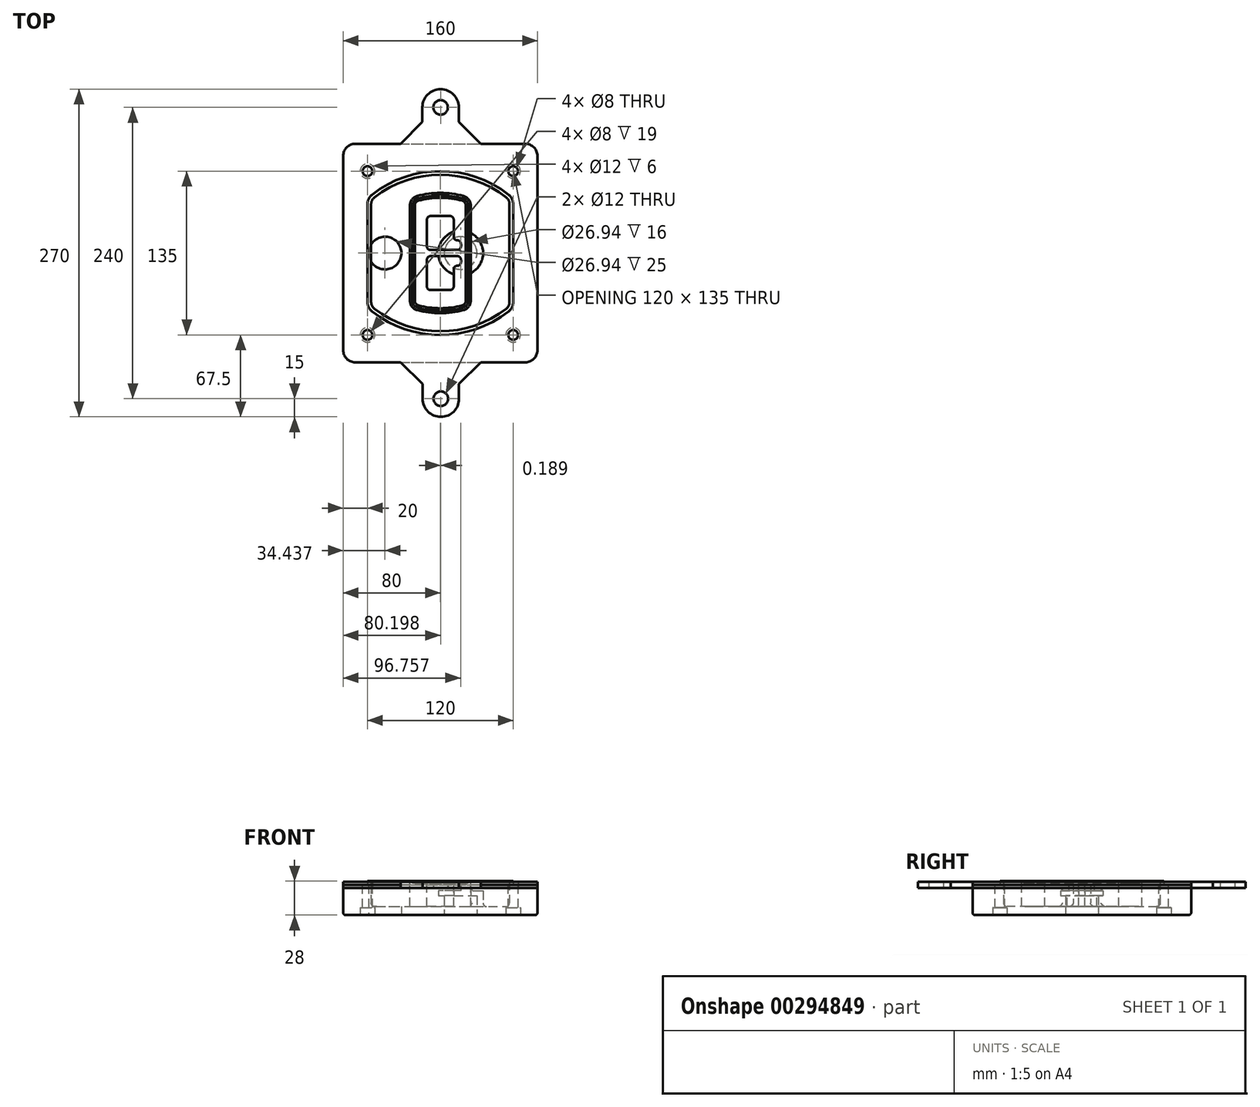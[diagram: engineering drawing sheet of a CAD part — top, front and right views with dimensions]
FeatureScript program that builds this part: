
annotation { "Feature Type Name" : "Feature", "Feature Type Description" : "" }
export const myFeature = defineFeature(function(context is Context, id is Id, definition is map)
    precondition{}
    {
        {
            var Q0;
            Q0=qCreatedBy(makeId("Top.planeOp"),FACE);
            var sketch = newSketch(context, id + "F0", { "sketchPlane" : qUnion([Q0])});
            skPoint(sketch, "E0.rect.middle", {"position": v(0, 0) * mm});
            skLineSegment(sketch, "E1.bottom", {"start": v(-70, -90) * mm, "end": v(70, -90) * mm});
            skLineSegment(sketch, "E1.top", {"start": v(-70, 90) * mm, "end": v(70, 90) * mm});
            skLineSegment(sketch, "E1.left", {"start": v(-80, -80) * mm, "end": v(-80, 80) * mm});
            skLineSegment(sketch, "E1.right", {"start": v(80, -80) * mm, "end": v(80, 80) * mm});
            skLineSegment(sketch, "E2", {"start": v(-80, 90) * mm, "end": v(80, -90) * mm, "construction": true});
            skLineSegment(sketch, "E3", {"start": v(80, 90) * mm, "end": v(-80, -90) * mm, "construction": true});
            skCircle(sketch, "E4", {"center": v(-60, 67.5) * mm, "radius": 4 * mm});
            skCircle(sketch, "E5", {"center": v(60, 67.5) * mm, "radius": 4 * mm});
            skCircle(sketch, "E6", {"center": v(60, -67.5) * mm, "radius": 4 * mm});
            skCircle(sketch, "E7", {"center": v(-60, -67.5) * mm, "radius": 4 * mm});
            skLineSegment(sketch, "E8", {"start": v(-60, 67.5) * mm, "end": v(60, 67.5) * mm, "construction": true});
            skLineSegment(sketch, "E9", {"start": v(60, 67.5) * mm, "end": v(60, -67.5) * mm, "construction": true});
            skLineSegment(sketch, "E10", {"start": v(60, -67.5) * mm, "end": v(-60, -67.5) * mm, "construction": true});
            skLineSegment(sketch, "E11", {"start": v(-60, -67.5) * mm, "end": v(-60, 67.5) * mm, "construction": true});
            skLineSegment(sketch, "E12", {"start": v(-60, 40.3) * mm, "end": v(-60, -40.3) * mm});
            skLineSegment(sketch, "E13", {"start": v(60, 40.3) * mm, "end": v(60, -40.3) * mm});
            skArc(sketch, "E14", {"start": v(56.15, 48.18) * mm, "mid": v(0, 67.5) * mm, "end": v(-56.15, 48.18) * mm});
            skArc(sketch, "E15", {"start": v(-56.15, -48.18) * mm, "mid": v(0, -67.5) * mm, "end": v(56.15, -48.18) * mm});
            skLineSegment(sketch, "E16", {"start": v(-60, 0) * mm, "end": v(60, 0) * mm, "construction": true});
            skPoint(sketch, "E17.visualSharp", {"position": v(-60, -45) * mm});
            skArc(sketch, "E17.filletArc", {"start": v(-60, -40.3) * mm, "mid": v(-58.99, -44.68) * mm, "end": v(-56.15, -48.18) * mm});
            skPoint(sketch, "E18.visualSharp", {"position": v(-60, 45) * mm});
            skArc(sketch, "E18.filletArc", {"start": v(-56.15, 48.18) * mm, "mid": v(-58.99, 44.68) * mm, "end": v(-60, 40.3) * mm});
            skPoint(sketch, "E19.visualSharp", {"position": v(60, 45) * mm});
            skArc(sketch, "E19.filletArc", {"start": v(60, 40.3) * mm, "mid": v(58.99, 44.68) * mm, "end": v(56.15, 48.18) * mm});
            skPoint(sketch, "E20.visualSharp", {"position": v(60, -45) * mm});
            skArc(sketch, "E20.filletArc", {"start": v(56.15, -48.18) * mm, "mid": v(58.99, -44.68) * mm, "end": v(60, -40.3) * mm});
            skPoint(sketch, "E21.visualSharp", {"position": v(-80, 90) * mm});
            skArc(sketch, "E21.filletArc", {"start": v(-70, 90) * mm, "mid": v(-77.07, 87.07) * mm, "end": v(-80, 80) * mm});
            skPoint(sketch, "E22.visualSharp", {"position": v(80, 90) * mm});
            skArc(sketch, "E22.filletArc", {"start": v(80, 80) * mm, "mid": v(77.07, 87.07) * mm, "end": v(70, 90) * mm});
            skPoint(sketch, "E23.visualSharp", {"position": v(80, -90) * mm});
            skArc(sketch, "E23.filletArc", {"start": v(70, -90) * mm, "mid": v(77.07, -87.07) * mm, "end": v(80, -80) * mm});
            skPoint(sketch, "E24.visualSharp", {"position": v(-80, -90) * mm});
            skArc(sketch, "E24.filletArc", {"start": v(-80, -80) * mm, "mid": v(-77.07, -87.07) * mm, "end": v(-70, -90) * mm});
            skArc(sketch, "E25.0", {"start": v(57, 40.3) * mm, "mid": v(56.3, 43.36) * mm, "end": v(54.3, 45.81) * mm});
            skLineSegment(sketch, "E25.1", {"start": v(57, 40.3) * mm, "end": v(57, -40.3) * mm});
            skArc(sketch, "E25.2", {"start": v(54.3, -45.81) * mm, "mid": v(56.3, -43.36) * mm, "end": v(57, -40.3) * mm});
            skArc(sketch, "E25.3", {"start": v(-54.3, -45.81) * mm, "mid": v(0, -64.5) * mm, "end": v(54.3, -45.81) * mm});
            skArc(sketch, "E25.4", {"start": v(-57, -40.3) * mm, "mid": v(-56.3, -43.36) * mm, "end": v(-54.3, -45.81) * mm});
            skArc(sketch, "E25.5", {"start": v(54.3, 45.81) * mm, "mid": v(0, 64.5) * mm, "end": v(-54.3, 45.81) * mm});
            skLineSegment(sketch, "E25.6", {"start": v(-57, 40.3) * mm, "end": v(-57, -40.3) * mm});
            skArc(sketch, "E25.7", {"start": v(-54.3, 45.81) * mm, "mid": v(-56.3, 43.36) * mm, "end": v(-57, 40.3) * mm});
            skArc(sketch, "E26.0", {"start": v(-58.62, 51.33) * mm, "mid": v(-62.58, 46.43) * mm, "end": v(-64, 40.3) * mm});
            skArc(sketch, "E26.1", {"start": v(58.62, 51.33) * mm, "mid": v(0, 71.5) * mm, "end": v(-58.62, 51.33) * mm});
            skArc(sketch, "E26.2", {"start": v(64, 40.3) * mm, "mid": v(62.58, 46.43) * mm, "end": v(58.62, 51.33) * mm});
            skLineSegment(sketch, "E26.3", {"start": v(64, 40.3) * mm, "end": v(64, -40.3) * mm});
            skArc(sketch, "E26.4", {"start": v(58.62, -51.33) * mm, "mid": v(62.58, -46.43) * mm, "end": v(64, -40.3) * mm});
            skLineSegment(sketch, "E26.5", {"start": v(-64, 40.3) * mm, "end": v(-64, -40.3) * mm});
            skArc(sketch, "E26.6", {"start": v(-58.62, -51.33) * mm, "mid": v(0, -71.5) * mm, "end": v(58.62, -51.33) * mm});
            skArc(sketch, "E26.7", {"start": v(-64, -40.3) * mm, "mid": v(-62.58, -46.43) * mm, "end": v(-58.62, -51.33) * mm});
            skSolve(sketch);
        }
        {
            var Q0;
            Q0=makeQuery(id+"F0.imprint","IMPRINT",FACE,{"disambiguationData":[TD([[makeQuery(id+"F0.imprint","IMPRINT",EDGE,{"derivedFrom":sQuery(id+"F0.wireOp",EDGE,"E1.bottom")}),1.0]])]});
            var Q1;
            Q1=makeQuery(id+"F0.imprint","IMPRINT",FACE,{"disambiguationData":[TD([[makeQuery(id+"F0.imprint","IMPRINT",EDGE,{"derivedFrom":sQuery(id+"F0.wireOp",EDGE,"E12")}),1.0]])]});
            var Q2;
            Q2=makeQuery(id+"F0.imprint","IMPRINT",FACE,{"disambiguationData":[TD([[makeQuery(id+"F0.imprint","IMPRINT",EDGE,{"derivedFrom":sQuery(id+"F0.wireOp",EDGE,"E25.0")}),1.0]])]});
            var Q3;
            Q3=makeQuery(id+"F0.imprint","IMPRINT",FACE,{"disambiguationData":[TD([[makeQuery(id+"F0.imprint","IMPRINT",EDGE,{"derivedFrom":sQuery(id+"F0.wireOp",EDGE,"E12")}),-1.0]])]});
            extrude(context, id + "F1", {"entities" : qUnion([Q0, Q1, Q2, Q3]), "oppositeDirection" : true, "depth" : 25 * mm});
        }
        {
            var Q0;
            Q0=makeQuery(id+"F0.imprint","IMPRINT",FACE,{"disambiguationData":[TD([[makeQuery(id+"F0.imprint","IMPRINT",EDGE,{"derivedFrom":sQuery(id+"F0.wireOp",EDGE,"E12")}),1.0]])]});
            extrude(context, id + "F2", {"entities" : qUnion([Q0]), "operationType" : NewBodyOperationType.ADD, "depth" : 3 * mm});
        }
        {
            var Q0;
            Q0=makeQuery(id+"F0.imprint","IMPRINT",FACE,{"disambiguationData":[TD([[makeQuery(id+"F0.imprint","IMPRINT",EDGE,{"derivedFrom":sQuery(id+"F0.wireOp",EDGE,"E25.0")}),1.0]])]});
            extrude(context, id + "F3", {"entities" : qUnion([Q0]), "operationType" : NewBodyOperationType.REMOVE, "oppositeDirection" : true, "depth" : 18 * mm});
        }
        {
            var Q0;
            Q0=makeQuery(id+"F2.opExtrude","CAP_FACE",FACE,{"disambiguationData":[OSD([sQuery(id+"F0.wireOp",EDGE,"E12"),sQuery(id+"F0.wireOp",EDGE,"E13"),sQuery(id+"F0.wireOp",EDGE,"E14"),sQuery(id+"F0.wireOp",EDGE,"E15"),sQuery(id+"F0.wireOp",EDGE,"E17.filletArc"),sQuery(id+"F0.wireOp",EDGE,"E18.filletArc"),sQuery(id+"F0.wireOp",EDGE,"E19.filletArc"),sQuery(id+"F0.wireOp",EDGE,"E20.filletArc"),sQuery(id+"F0.wireOp",EDGE,"E25.0"),sQuery(id+"F0.wireOp",EDGE,"E25.1"),sQuery(id+"F0.wireOp",EDGE,"E25.2"),sQuery(id+"F0.wireOp",EDGE,"E25.3"),sQuery(id+"F0.wireOp",EDGE,"E25.4"),sQuery(id+"F0.wireOp",EDGE,"E25.5"),sQuery(id+"F0.wireOp",EDGE,"E25.6"),sQuery(id+"F0.wireOp",EDGE,"E25.7")])],"isStart":false});
            var sketch = newSketch(context, id + "F4", { "sketchPlane" : qUnion([Q0])});
            skArc(sketch, "E27.0", {"start": v(-19.08, -46.97) * mm, "mid": v(0, -49.5) * mm, "end": v(19.08, -46.97) * mm});
            skArc(sketch, "E28.0", {"start": v(19.08, 46.97) * mm, "mid": v(0, 49.5) * mm, "end": v(-19.08, 46.97) * mm});
            skLineSegment(sketch, "E29", {"start": v(-25, 39.25) * mm, "end": v(-25, -39.25) * mm});
            skLineSegment(sketch, "E30", {"start": v(25, 39.25) * mm, "end": v(25, -39.25) * mm});
            skLineSegment(sketch, "E31", {"start": v(-25, 45.1) * mm, "end": v(25, 45.1) * mm, "construction": true});
            skLineSegment(sketch, "E32", {"start": v(-25, -45.1) * mm, "end": v(25, -45.1) * mm, "construction": true});
            skPoint(sketch, "E33.visualSharp", {"position": v(-25, 45.1) * mm});
            skArc(sketch, "E33.filletArc", {"start": v(-19.08, 46.97) * mm, "mid": v(-23.35, 44.11) * mm, "end": v(-25, 39.25) * mm});
            skPoint(sketch, "E34.visualSharp", {"position": v(25, 45.1) * mm});
            skArc(sketch, "E34.filletArc", {"start": v(25, 39.25) * mm, "mid": v(23.35, 44.11) * mm, "end": v(19.08, 46.97) * mm});
            skPoint(sketch, "E35.visualSharp", {"position": v(25, -45.1) * mm});
            skArc(sketch, "E35.filletArc", {"start": v(19.08, -46.97) * mm, "mid": v(23.35, -44.11) * mm, "end": v(25, -39.25) * mm});
            skPoint(sketch, "E36.visualSharp", {"position": v(-25, -45.1) * mm});
            skArc(sketch, "E36.filletArc", {"start": v(-25, -39.25) * mm, "mid": v(-23.35, -44.11) * mm, "end": v(-19.08, -46.97) * mm});
            skArc(sketch, "E37.0", {"start": v(54.3, 45.81) * mm, "mid": v(0, 64.5) * mm, "end": v(-54.3, 45.81) * mm});
            skArc(sketch, "E37.1", {"start": v(-54.3, 45.81) * mm, "mid": v(-56.3, 43.36) * mm, "end": v(-57, 40.3) * mm});
            skLineSegment(sketch, "E37.2", {"start": v(-57, 40.3) * mm, "end": v(-57, -40.3) * mm});
            skArc(sketch, "E37.3", {"start": v(-57, -40.3) * mm, "mid": v(-56.3, -43.36) * mm, "end": v(-54.3, -45.81) * mm});
            skArc(sketch, "E37.4", {"start": v(-54.3, -45.81) * mm, "mid": v(0, -64.5) * mm, "end": v(54.3, -45.81) * mm});
            skArc(sketch, "E37.5", {"start": v(54.3, -45.81) * mm, "mid": v(56.3, -43.36) * mm, "end": v(57, -40.3) * mm});
            skLineSegment(sketch, "E37.6", {"start": v(57, 40.3) * mm, "end": v(57, -40.3) * mm});
            skArc(sketch, "E37.7", {"start": v(57, 40.3) * mm, "mid": v(56.3, 43.36) * mm, "end": v(54.3, 45.81) * mm});
            skLineSegment(sketch, "E38.0", {"start": v(23, 39.25) * mm, "end": v(23, -39.25) * mm});
            skArc(sketch, "E38.1", {"start": v(18.56, -45.04) * mm, "mid": v(21.76, -42.9) * mm, "end": v(23, -39.25) * mm});
            skArc(sketch, "E38.2", {"start": v(-18.56, -45.04) * mm, "mid": v(0, -47.5) * mm, "end": v(18.56, -45.04) * mm});
            skArc(sketch, "E38.3", {"start": v(-23, -39.25) * mm, "mid": v(-21.76, -42.9) * mm, "end": v(-18.56, -45.04) * mm});
            skLineSegment(sketch, "E38.4", {"start": v(-23, 39.25) * mm, "end": v(-23, -39.25) * mm});
            skArc(sketch, "E38.5", {"start": v(23, 39.25) * mm, "mid": v(21.76, 42.9) * mm, "end": v(18.56, 45.04) * mm});
            skArc(sketch, "E38.6", {"start": v(-18.56, 45.04) * mm, "mid": v(-21.76, 42.9) * mm, "end": v(-23, 39.25) * mm});
            skArc(sketch, "E38.7", {"start": v(18.56, 45.04) * mm, "mid": v(0, 47.5) * mm, "end": v(-18.56, 45.04) * mm});
            skArc(sketch, "E39.0", {"start": v(21, 39.25) * mm, "mid": v(20.18, 41.68) * mm, "end": v(18.04, 43.1) * mm});
            skLineSegment(sketch, "E39.1", {"start": v(21, 39.25) * mm, "end": v(21, -39.25) * mm});
            skArc(sketch, "E39.2", {"start": v(18.04, -43.1) * mm, "mid": v(20.18, -41.68) * mm, "end": v(21, -39.25) * mm});
            skArc(sketch, "E39.3", {"start": v(-18.04, -43.1) * mm, "mid": v(0, -45.5) * mm, "end": v(18.04, -43.1) * mm});
            skArc(sketch, "E39.4", {"start": v(-21, -39.25) * mm, "mid": v(-20.18, -41.68) * mm, "end": v(-18.04, -43.1) * mm});
            skArc(sketch, "E39.5", {"start": v(18.04, 43.1) * mm, "mid": v(0, 45.5) * mm, "end": v(-18.04, 43.1) * mm});
            skLineSegment(sketch, "E39.6", {"start": v(-21, 39.25) * mm, "end": v(-21, -39.25) * mm});
            skArc(sketch, "E39.7", {"start": v(-18.04, 43.1) * mm, "mid": v(-20.18, 41.68) * mm, "end": v(-21, 39.25) * mm});
            skLineSegment(sketch, "E40", {"start": v(-25, 0) * mm, "end": v(25, 0) * mm, "construction": true});
            skLineSegment(sketch, "E41", {"start": v(-11, 5.5) * mm, "end": v(-11, 27.5) * mm});
            skLineSegment(sketch, "E42", {"start": v(-8, 30.5) * mm, "end": v(8, 30.5) * mm});
            skLineSegment(sketch, "E43", {"start": v(11, 27.5) * mm, "end": v(11, 13.5) * mm});
            skLineSegment(sketch, "E44", {"start": v(14, 10.5) * mm, "end": v(14, 10.5) * mm});
            skLineSegment(sketch, "E45", {"start": v(17, 7.5) * mm, "end": v(17, 5.5) * mm});
            skLineSegment(sketch, "E46", {"start": v(14, 2.5) * mm, "end": v(-8, 2.5) * mm});
            skPoint(sketch, "E47.visualSharp", {"position": v(-11, 30.5) * mm});
            skArc(sketch, "E47.filletArc", {"start": v(-8, 30.5) * mm, "mid": v(-10.12, 29.62) * mm, "end": v(-11, 27.5) * mm});
            skPoint(sketch, "E48.visualSharp", {"position": v(11, 30.5) * mm});
            skArc(sketch, "E48.filletArc", {"start": v(11, 27.5) * mm, "mid": v(10.12, 29.62) * mm, "end": v(8, 30.5) * mm});
            skPoint(sketch, "E49.visualSharp", {"position": v(11, 10.5) * mm});
            skArc(sketch, "E49.filletArc", {"start": v(11, 13.5) * mm, "mid": v(11.88, 11.38) * mm, "end": v(14, 10.5) * mm});
            skPoint(sketch, "E50.visualSharp", {"position": v(17, 10.5) * mm});
            skArc(sketch, "E50.filletArc", {"start": v(17, 7.5) * mm, "mid": v(16.12, 9.62) * mm, "end": v(14, 10.5) * mm});
            skPoint(sketch, "E51.visualSharp", {"position": v(17, 2.5) * mm});
            skArc(sketch, "E51.filletArc", {"start": v(14, 2.5) * mm, "mid": v(16.12, 3.38) * mm, "end": v(17, 5.5) * mm});
            skPoint(sketch, "E52.visualSharp", {"position": v(-11, 2.5) * mm});
            skArc(sketch, "E52.filletArc", {"start": v(-11, 5.5) * mm, "mid": v(-10.12, 3.38) * mm, "end": v(-8, 2.5) * mm});
            skLineSegment(sketch, "E53.0.MirrorCS", {"start": v(14, -2.5) * mm, "end": v(-8, -2.5) * mm});
            skArc(sketch, "E54.0.MirrorCS", {"start": v(-11, -5.5) * mm, "mid": v(-10.12, -3.38) * mm, "end": v(-8, -2.5) * mm});
            skLineSegment(sketch, "E55.0.MirrorCS", {"start": v(-11, -5.5) * mm, "end": v(-11, -27.5) * mm});
            skArc(sketch, "E56.0.MirrorCS", {"start": v(-8, -30.5) * mm, "mid": v(-10.12, -29.62) * mm, "end": v(-11, -27.5) * mm});
            skLineSegment(sketch, "E57.0.MirrorCS", {"start": v(-8, -30.5) * mm, "end": v(8, -30.5) * mm});
            skArc(sketch, "E58.0.MirrorCS", {"start": v(11, -27.5) * mm, "mid": v(10.12, -29.62) * mm, "end": v(8, -30.5) * mm});
            skLineSegment(sketch, "E59.0.MirrorCS", {"start": v(11, -27.5) * mm, "end": v(11, -13.5) * mm});
            skArc(sketch, "E60.0.MirrorCS", {"start": v(11, -13.5) * mm, "mid": v(11.88, -11.38) * mm, "end": v(14, -10.5) * mm});
            skArc(sketch, "E61.0.MirrorCS", {"start": v(17, -7.5) * mm, "mid": v(16.12, -9.62) * mm, "end": v(14, -10.5) * mm});
            skLineSegment(sketch, "E62.0.MirrorCS", {"start": v(17, -7.5) * mm, "end": v(17, -5.5) * mm});
            skArc(sketch, "E63.0.MirrorCS", {"start": v(14, -2.5) * mm, "mid": v(16.12, -3.38) * mm, "end": v(17, -5.5) * mm});
            skSolve(sketch);
        }
        {
            var Q0;
            Q0=makeQuery(id+"F4.imprint","IMPRINT",FACE,{"disambiguationData":[TD([[makeQuery(id+"F4.imprint","IMPRINT",EDGE,{"derivedFrom":sQuery(id+"F4.wireOp",EDGE,"E27.0")}),1.0]])]});
            var Q1;
            Q1=makeQuery(id+"F4.imprint","IMPRINT",FACE,{"disambiguationData":[TD([[makeQuery(id+"F4.imprint","IMPRINT",EDGE,{"derivedFrom":sQuery(id+"F4.wireOp",EDGE,"E38.0")}),-1.0]])]});
            var Q2;
            Q2=makeQuery(id+"F4.imprint","IMPRINT",FACE,{"disambiguationData":[TD([[makeQuery(id+"F4.imprint","IMPRINT",EDGE,{"derivedFrom":sQuery(id+"F4.wireOp",EDGE,"E39.0")}),1.0]])]});
            extrude(context, id + "F5", {"entities" : qUnion([Q0, Q1, Q2]), "operationType" : NewBodyOperationType.ADD, "endBound" : BoundingType.UP_TO_NEXT, "oppositeDirection" : true, "depth" : 25 * mm});
        }
        {
            var Q0;
            Q0=makeQuery(id+"F4.imprint","IMPRINT",FACE,{"disambiguationData":[TD([[makeQuery(id+"F4.imprint","IMPRINT",EDGE,{"derivedFrom":sQuery(id+"F4.wireOp",EDGE,"E38.0")}),-1.0]])]});
            extrude(context, id + "F6", {"entities" : qUnion([Q0]), "operationType" : NewBodyOperationType.REMOVE, "oppositeDirection" : true, "depth" : 2 * mm});
        }
        {
            var Q0;
            Q0=makeQuery(id+"F1.opExtrude","CAP_FACE",FACE,{"disambiguationData":[OSD([sQuery(id+"F0.wireOp",EDGE,"E1.bottom"),sQuery(id+"F0.wireOp",EDGE,"E1.top"),sQuery(id+"F0.wireOp",EDGE,"E1.left"),sQuery(id+"F0.wireOp",EDGE,"E1.right"),sQuery(id+"F0.wireOp",EDGE,"E4"),sQuery(id+"F0.wireOp",EDGE,"E5"),sQuery(id+"F0.wireOp",EDGE,"E6"),sQuery(id+"F0.wireOp",EDGE,"E7"),sQuery(id+"F0.wireOp",EDGE,"E21.filletArc"),sQuery(id+"F0.wireOp",EDGE,"E22.filletArc"),sQuery(id+"F0.wireOp",EDGE,"E23.filletArc"),sQuery(id+"F0.wireOp",EDGE,"E24.filletArc")])],"isStart":false});
            var sketch = newSketch(context, id + "F7", { "sketchPlane" : qUnion([Q0])});
            skCircle(sketch, "E64", {"center": v(16.76, 0) * mm, "radius": 13.47 * mm});
            skCircle(sketch, "E65", {"center": v(-45.56, 0) * mm, "radius": 13.47 * mm});
            skLineSegment(sketch, "E66", {"start": v(80, 0) * mm, "end": v(-80, 0) * mm});
            skCircle(sketch, "E67", {"center": v(16.76, 0) * mm, "radius": 18.47 * mm});
            skCircle(sketch, "E68", {"center": v(60, -67.5) * mm, "radius": 6 * mm});
            skCircle(sketch, "E69", {"center": v(-60, -67.5) * mm, "radius": 6 * mm});
            skCircle(sketch, "E70", {"center": v(-60, 67.5) * mm, "radius": 6 * mm});
            skCircle(sketch, "E71", {"center": v(60, 67.5) * mm, "radius": 6 * mm});
            skSolve(sketch);
        }
        {
            var Q0;
            {var subQ1=sQuery(id+"F7.wireOp",EDGE,"E66");var subQ4=sQuery(id+"F7.wireOp",EDGE,"E64");var subQ6=makeQuery(id+"F7.imprint","INTERSECT",VERTEX,{"disambiguationData":[OD(0.0)],"derivedFrom":[subQ4,subQ1]});Q0=makeQuery(id+"F7.imprint","IMPRINT",FACE,{"disambiguationData":[TD([[makeQuery(id+"F7.imprint","IMPRINT",EDGE,{"disambiguationData":[TD([[subQ6,-1.0]])],"derivedFrom":subQ4}),-1.0]])]});}
            var Q1;
            {var subQ0=sQuery(id+"F7.wireOp",EDGE,"E66");var subQ1=sQuery(id+"F7.wireOp",EDGE,"E64");var subQ3=makeQuery(id+"F7.imprint","INTERSECT",VERTEX,{"disambiguationData":[OD(0.0)],"derivedFrom":[subQ1,subQ0]});Q1=makeQuery(id+"F7.imprint","IMPRINT",FACE,{"disambiguationData":[TD([[makeQuery(id+"F7.imprint","IMPRINT",EDGE,{"disambiguationData":[TD([[subQ3,-1.0]])],"derivedFrom":subQ1}),1.0]])]});}
            var Q2;
            {var subQ0=sQuery(id+"F7.wireOp",EDGE,"E66");var subQ1=sQuery(id+"F7.wireOp",EDGE,"E64");var subQ3=makeQuery(id+"F7.imprint","INTERSECT",VERTEX,{"disambiguationData":[OD(0.0)],"derivedFrom":[subQ1,subQ0]});Q2=makeQuery(id+"F7.imprint","IMPRINT",FACE,{"disambiguationData":[TD([[makeQuery(id+"F7.imprint","IMPRINT",EDGE,{"disambiguationData":[TD([[subQ3,1.0]])],"derivedFrom":subQ1}),1.0]])]});}
            var Q3;
            {var subQ1=sQuery(id+"F7.wireOp",EDGE,"E66");var subQ4=sQuery(id+"F7.wireOp",EDGE,"E64");var subQ6=makeQuery(id+"F7.imprint","INTERSECT",VERTEX,{"disambiguationData":[OD(0.0)],"derivedFrom":[subQ4,subQ1]});Q3=makeQuery(id+"F7.imprint","IMPRINT",FACE,{"disambiguationData":[TD([[makeQuery(id+"F7.imprint","IMPRINT",EDGE,{"disambiguationData":[TD([[subQ6,1.0]])],"derivedFrom":subQ4}),-1.0]])]});}
            extrude(context, id + "F8", {"entities" : qUnion([Q0, Q1, Q2, Q3]), "operationType" : NewBodyOperationType.ADD, "oppositeDirection" : true, "depth" : 20 * mm});
        }
        {
            var Q0;
            {var subQ0=sQuery(id+"F7.wireOp",EDGE,"E66");var subQ1=sQuery(id+"F7.wireOp",EDGE,"E64");var subQ3=makeQuery(id+"F7.imprint","INTERSECT",VERTEX,{"disambiguationData":[OD(0.0)],"derivedFrom":[subQ1,subQ0]});Q0=makeQuery(id+"F7.imprint","IMPRINT",FACE,{"disambiguationData":[TD([[makeQuery(id+"F7.imprint","IMPRINT",EDGE,{"disambiguationData":[TD([[subQ3,-1.0]])],"derivedFrom":subQ1}),1.0]])]});}
            var Q1;
            {var subQ0=sQuery(id+"F7.wireOp",EDGE,"E66");var subQ1=sQuery(id+"F7.wireOp",EDGE,"E64");var subQ3=makeQuery(id+"F7.imprint","INTERSECT",VERTEX,{"disambiguationData":[OD(0.0)],"derivedFrom":[subQ1,subQ0]});Q1=makeQuery(id+"F7.imprint","IMPRINT",FACE,{"disambiguationData":[TD([[makeQuery(id+"F7.imprint","IMPRINT",EDGE,{"disambiguationData":[TD([[subQ3,1.0]])],"derivedFrom":subQ1}),1.0]])]});}
            extrude(context, id + "F9", {"entities" : qUnion([Q0, Q1]), "operationType" : NewBodyOperationType.REMOVE, "oppositeDirection" : true, "depth" : 16 * mm});
        }
        {
            var Q0;
            {var subQ0=sQuery(id+"F7.wireOp",EDGE,"E66");var subQ1=sQuery(id+"F7.wireOp",EDGE,"E65");var subQ3=makeQuery(id+"F7.imprint","INTERSECT",VERTEX,{"disambiguationData":[OD(0.0)],"derivedFrom":[subQ1,subQ0]});Q0=makeQuery(id+"F7.imprint","IMPRINT",FACE,{"disambiguationData":[TD([[makeQuery(id+"F7.imprint","IMPRINT",EDGE,{"disambiguationData":[TD([[subQ3,-1.0]])],"derivedFrom":subQ1}),1.0]])]});}
            var Q1;
            {var subQ0=sQuery(id+"F7.wireOp",EDGE,"E66");var subQ1=sQuery(id+"F7.wireOp",EDGE,"E65");var subQ3=makeQuery(id+"F7.imprint","INTERSECT",VERTEX,{"disambiguationData":[OD(0.0)],"derivedFrom":[subQ1,subQ0]});Q1=makeQuery(id+"F7.imprint","IMPRINT",FACE,{"disambiguationData":[TD([[makeQuery(id+"F7.imprint","IMPRINT",EDGE,{"disambiguationData":[TD([[subQ3,1.0]])],"derivedFrom":subQ1}),1.0]])]});}
            extrude(context, id + "F10", {"entities" : qUnion([Q0, Q1]), "operationType" : NewBodyOperationType.REMOVE, "oppositeDirection" : true, "depth" : 25 * mm});
        }
        {
            var Q0;
            Q0=makeQuery(id+"F7.imprint","IMPRINT",FACE,{"disambiguationData":[TD([[makeQuery(id+"F7.imprint","IMPRINT",EDGE,{"derivedFrom":sQuery(id+"F7.wireOp",EDGE,"E68")}),1.0]])]});
            var Q1;
            Q1=makeQuery(id+"F7.imprint","IMPRINT",FACE,{"disambiguationData":[TD([[makeQuery(id+"F7.imprint","IMPRINT",EDGE,{"derivedFrom":makeQuery(id+"F1.opExtrude","CAP_EDGE",EDGE,{"disambiguationData":[OSD([sQuery(id+"F0.wireOp",EDGE,"E5")])],"isStart":false})}),-1.0]])]});
            var Q2;
            Q2=makeQuery(id+"F7.imprint","IMPRINT",FACE,{"disambiguationData":[TD([[makeQuery(id+"F7.imprint","IMPRINT",EDGE,{"derivedFrom":sQuery(id+"F7.wireOp",EDGE,"E69")}),1.0]])]});
            var Q3;
            Q3=makeQuery(id+"F7.imprint","IMPRINT",FACE,{"disambiguationData":[TD([[makeQuery(id+"F7.imprint","IMPRINT",EDGE,{"derivedFrom":makeQuery(id+"F1.opExtrude","CAP_EDGE",EDGE,{"disambiguationData":[OSD([sQuery(id+"F0.wireOp",EDGE,"E4")])],"isStart":false})}),-1.0]])]});
            var Q4;
            Q4=makeQuery(id+"F7.imprint","IMPRINT",FACE,{"disambiguationData":[TD([[makeQuery(id+"F7.imprint","IMPRINT",EDGE,{"derivedFrom":sQuery(id+"F7.wireOp",EDGE,"E70")}),1.0]])]});
            var Q5;
            Q5=makeQuery(id+"F7.imprint","IMPRINT",FACE,{"disambiguationData":[TD([[makeQuery(id+"F7.imprint","IMPRINT",EDGE,{"derivedFrom":makeQuery(id+"F1.opExtrude","CAP_EDGE",EDGE,{"disambiguationData":[OSD([sQuery(id+"F0.wireOp",EDGE,"E7")])],"isStart":false})}),-1.0]])]});
            var Q6;
            Q6=makeQuery(id+"F7.imprint","IMPRINT",FACE,{"disambiguationData":[TD([[makeQuery(id+"F7.imprint","IMPRINT",EDGE,{"derivedFrom":sQuery(id+"F7.wireOp",EDGE,"E71")}),1.0]])]});
            var Q7;
            Q7=makeQuery(id+"F7.imprint","IMPRINT",FACE,{"disambiguationData":[TD([[makeQuery(id+"F7.imprint","IMPRINT",EDGE,{"derivedFrom":makeQuery(id+"F1.opExtrude","CAP_EDGE",EDGE,{"disambiguationData":[OSD([sQuery(id+"F0.wireOp",EDGE,"E6")])],"isStart":false})}),-1.0]])]});
            extrude(context, id + "F11", {"entities" : qUnion([Q0, Q1, Q2, Q3, Q4, Q5, Q6, Q7]), "operationType" : NewBodyOperationType.REMOVE, "oppositeDirection" : true, "depth" : 6 * mm});
        }
        {
            var Q0;
            Q0=makeQuery(id+"F9.boolean.opBoolean","COPY",FACE,{"derivedFrom":makeQuery(id+"F9.opExtrude","CAP_FACE",FACE,{"disambiguationData":[OSD([sQuery(id+"F7.wireOp",EDGE,"E64")])],"isStart":false})});
            var sketch = newSketch(context, id + "F12", { "sketchPlane" : qUnion([Q0])});
            skArc(sketch, "E72.0", {"start": v(11, 17.55) * mm, "mid": v(2.57, 11.82) * mm, "end": v(-1.54, 2.5) * mm});
            skArc(sketch, "E72.1", {"start": v(-1.54, -2.5) * mm, "mid": v(2.57, -11.82) * mm, "end": v(11, -17.55) * mm});
            skLineSegment(sketch, "E73", {"start": v(-1.54, -2.5) * mm, "end": v(14, -2.5) * mm});
            skLineSegment(sketch, "E74.0", {"start": v(14, 2.5) * mm, "end": v(-1.54, 2.5) * mm});
            skArc(sketch, "E74.1", {"start": v(14, 2.5) * mm, "mid": v(16.12, 3.38) * mm, "end": v(17, 5.5) * mm});
            skLineSegment(sketch, "E74.2", {"start": v(17, 7.5) * mm, "end": v(17, 5.5) * mm});
            skArc(sketch, "E74.3", {"start": v(17, 7.5) * mm, "mid": v(16.12, 9.62) * mm, "end": v(14, 10.5) * mm});
            skArc(sketch, "E74.4", {"start": v(11, 13.5) * mm, "mid": v(11.88, 11.38) * mm, "end": v(14, 10.5) * mm});
            skLineSegment(sketch, "E74.5", {"start": v(11, 17.55) * mm, "end": v(11, 13.5) * mm});
            skLineSegment(sketch, "E74.7", {"start": v(14, -2.5) * mm, "end": v(-1.54, -2.5) * mm});
            skArc(sketch, "E74.8", {"start": v(14, -2.5) * mm, "mid": v(16.12, -3.38) * mm, "end": v(17, -5.5) * mm});
            skLineSegment(sketch, "E74.9", {"start": v(17, -7.5) * mm, "end": v(17, -5.5) * mm});
            skArc(sketch, "E74.10", {"start": v(17, -7.5) * mm, "mid": v(16.12, -9.62) * mm, "end": v(14, -10.5) * mm});
            skArc(sketch, "E74.11", {"start": v(11, -13.5) * mm, "mid": v(11.88, -11.38) * mm, "end": v(14, -10.5) * mm});
            skLineSegment(sketch, "E74.12", {"start": v(11, -17.55) * mm, "end": v(11, -13.5) * mm});
            skPoint(sketch, "E75.orphan", {"position": v(11, -27.5) * mm});
            skPoint(sketch, "E76.orphan", {"position": v(-8, -2.5) * mm});
            skPoint(sketch, "E77.orphan", {"position": v(-8, 2.5) * mm});
            skPoint(sketch, "E78.orphan", {"position": v(11, 27.5) * mm});
            skSolve(sketch);
        }
        {
            var Q0;
            {var subQ7=sQuery(id+"F12.wireOp",EDGE,"E72.0");var subQ14=sQuery(id+"F12.wireOp",EDGE,"E72.1");var subQ16=sQuery(id+"F12.wireOp",EDGE,"E74.1");var subQ18=sQuery(id+"F12.wireOp",EDGE,"E74.8");Q0=qUnion([makeQuery(id+"F12.imprint","IMPRINT",FACE,{"disambiguationData":[TD([[makeQuery(id+"F12.imprint","IMPRINT",EDGE,{"derivedFrom":subQ7}),1.0]])]}),makeQuery(id+"F12.imprint","IMPRINT",FACE,{"disambiguationData":[TD([[makeQuery(id+"F12.imprint","IMPRINT",EDGE,{"derivedFrom":subQ14}),1.0]])]}),makeQuery(id+"F12.imprint","IMPRINT",FACE,{"disambiguationData":[TD([[makeQuery(id+"F12.imprint","IMPRINT",EDGE,{"derivedFrom":subQ16}),1.0]])]}),makeQuery(id+"F12.imprint","IMPRINT",FACE,{"disambiguationData":[TD([[makeQuery(id+"F12.imprint","IMPRINT",EDGE,{"derivedFrom":subQ18}),-1.0]])]})]);}
            var Q1;
            Q1=makeQuery(id+"F5.boolean.opBoolean","SPLIT",FACE,{"disambiguationData":[TD([makeQuery(id+"F5.opExtrude","SWEPT_FACE",FACE,{"disambiguationData":[OSD([sQuery(id+"F4.wireOp",EDGE,"E41")])]})])],"derivedFrom":makeQuery(id+"F3.boolean.opBoolean","COPY",FACE,{"derivedFrom":makeQuery(id+"F3.opExtrude","CAP_FACE",FACE,{"disambiguationData":[OSD([sQuery(id+"F0.wireOp",EDGE,"E25.0"),sQuery(id+"F0.wireOp",EDGE,"E25.1"),sQuery(id+"F0.wireOp",EDGE,"E25.2"),sQuery(id+"F0.wireOp",EDGE,"E25.3"),sQuery(id+"F0.wireOp",EDGE,"E25.4"),sQuery(id+"F0.wireOp",EDGE,"E25.5"),sQuery(id+"F0.wireOp",EDGE,"E25.6"),sQuery(id+"F0.wireOp",EDGE,"E25.7")])],"isStart":false})})});
            extrude(context, id + "F13", {"entities" : qUnion([Q0]), "operationType" : NewBodyOperationType.REMOVE, "endBound" : BoundingType.UP_TO_SURFACE, "endBoundEntityFace" : qUnion([Q1]), "depth" : 25 * mm});
        }
        {
            var Q0;
            Q0=makeQuery(id+"F3.boolean.opBoolean","COPY",EDGE,{"derivedFrom":makeQuery(id+"F3.opExtrude","CAP_EDGE",EDGE,{"disambiguationData":[OSD([sQuery(id+"F0.wireOp",EDGE,"E25.6")])],"isStart":false})});
            var Q1;
            Q1=makeQuery(id+"F8.boolean.opBoolean","INTERSECT",EDGE,{"derivedFrom":[makeQuery(id+"F5.opExtrude","SWEPT_FACE",FACE,{"disambiguationData":[OSD([sQuery(id+"F4.wireOp",EDGE,"E30")])]}),makeQuery(id+"F8.opExtrude","CAP_FACE",FACE,{"disambiguationData":[OSD([sQuery(id+"F7.wireOp",EDGE,"E67")])],"isStart":false})]});
            var Q2;
            Q2=makeQuery(id+"F8.boolean.opBoolean","INTERSECT",EDGE,{"disambiguationData":[OD(1.0)],"derivedFrom":[makeQuery(id+"F5.opExtrude","SWEPT_FACE",FACE,{"disambiguationData":[OSD([sQuery(id+"F4.wireOp",EDGE,"E30")])]}),makeQuery(id+"F8.opExtrude","SWEPT_FACE",FACE,{"disambiguationData":[OSD([sQuery(id+"F7.wireOp",EDGE,"E67")])]})]});
            var Q3;
            {var subQ0=sQuery(id+"F4.wireOp",EDGE,"E30");Q3=makeQuery(id+"F8.boolean.opBoolean","SPLIT",EDGE,{"disambiguationData":[TD([makeQuery(id+"F5.opExtrude","SWEPT_FACE",FACE,{"disambiguationData":[OSD([sQuery(id+"F4.wireOp",EDGE,"E35.filletArc")])]})])],"derivedFrom":makeQuery(id+"F5.opExtrude","CAP_EDGE",EDGE,{"disambiguationData":[OSD([subQ0])],"isStart":false})});}
            var Q4;
            {var subQ0=sQuery(id+"F0.wireOp",EDGE,"E25.7");var subQ1=sQuery(id+"F0.wireOp",EDGE,"E25.1");var subQ2=sQuery(id+"F0.wireOp",EDGE,"E25.6");var subQ3=sQuery(id+"F0.wireOp",EDGE,"E25.5");var subQ4=sQuery(id+"F0.wireOp",EDGE,"E25.4");var subQ5=sQuery(id+"F0.wireOp",EDGE,"E25.0");var subQ6=sQuery(id+"F0.wireOp",EDGE,"E25.2");var subQ7=sQuery(id+"F0.wireOp",EDGE,"E25.3");Q4=makeQuery(id+"F8.boolean.opBoolean","INTERSECT",EDGE,{"derivedFrom":[makeQuery(id+"F5.boolean.opBoolean","SPLIT",FACE,{"disambiguationData":[TD([makeQuery(id+"F2.opExtrude","SWEPT_FACE",FACE,{"disambiguationData":[OSD([subQ5])]})])],"derivedFrom":makeQuery(id+"F3.boolean.opBoolean","COPY",FACE,{"derivedFrom":makeQuery(id+"F3.opExtrude","CAP_FACE",FACE,{"disambiguationData":[OSD([subQ5,subQ1,subQ6,subQ7,subQ4,subQ3,subQ2,subQ0])],"isStart":false})})}),makeQuery(id+"F8.opExtrude","SWEPT_FACE",FACE,{"disambiguationData":[OSD([sQuery(id+"F7.wireOp",EDGE,"E67")])]})]});}
            var Q5;
            Q5=makeQuery(id+"F8.boolean.opBoolean","INTERSECT",EDGE,{"disambiguationData":[OD(0.0)],"derivedFrom":[makeQuery(id+"F5.opExtrude","SWEPT_FACE",FACE,{"disambiguationData":[OSD([sQuery(id+"F4.wireOp",EDGE,"E30")])]}),makeQuery(id+"F8.opExtrude","SWEPT_FACE",FACE,{"disambiguationData":[OSD([sQuery(id+"F7.wireOp",EDGE,"E67")])]})]});
            fillet(context, id + "F14", {"entities" : qUnion([Q0, Q1, Q2, Q3, Q4, Q5]), "radius" : 3 * mm, "tangentPropagation" : true, "allowEdgeOverflow" : false});
        }
        {
            var Q0;
            Q0=makeQuery(id+"F1.opExtrude","CAP_EDGE",EDGE,{"disambiguationData":[OSD([sQuery(id+"F0.wireOp",EDGE,"E1.bottom")])],"isStart":false});
            fillet(context, id + "F15", {"entities" : qUnion([Q0]), "radius" : 2 * mm, "tangentPropagation" : true, "allowEdgeOverflow" : false});
        }
        {
            var Q0;
            {var subQ0=sQuery(id+"F0.wireOp",EDGE,"E21.filletArc");var subQ1=sQuery(id+"F0.wireOp",EDGE,"E7");var subQ2=sQuery(id+"F0.wireOp",EDGE,"E6");var subQ3=sQuery(id+"F0.wireOp",EDGE,"E5");var subQ4=sQuery(id+"F0.wireOp",EDGE,"E4");var subQ5=sQuery(id+"F0.wireOp",EDGE,"E22.filletArc");var subQ6=sQuery(id+"F0.wireOp",EDGE,"E1.bottom");var subQ7=sQuery(id+"F0.wireOp",EDGE,"E1.right");var subQ8=sQuery(id+"F0.wireOp",EDGE,"E1.top");var subQ9=sQuery(id+"F0.wireOp",EDGE,"E1.left");var subQ10=sQuery(id+"F0.wireOp",EDGE,"E23.filletArc");var subQ11=sQuery(id+"F0.wireOp",EDGE,"E24.filletArc");Q0=makeQuery(id+"F2.boolean.opBoolean","SPLIT",FACE,{"disambiguationData":[TD([makeQuery(id+"F1.opExtrude","SWEPT_FACE",FACE,{"disambiguationData":[OSD([subQ6])]})])],"derivedFrom":makeQuery(id+"F1.opExtrude","CAP_FACE",FACE,{"disambiguationData":[OSD([subQ6,subQ8,subQ9,subQ7,subQ4,subQ3,subQ2,subQ1,subQ0,subQ5,subQ10,subQ11])],"isStart":true})});}
            var sketch = newSketch(context, id + "F16", { "sketchPlane" : qUnion([Q0])});
            skLineSegment(sketch, "E79", {"start": v(-32.8, 90) * mm, "end": v(-14.8, 108) * mm});
            skLineSegment(sketch, "E80", {"start": v(-14.8, 108) * mm, "end": v(-14.8, 120) * mm});
            skLineSegment(sketch, "E81", {"start": v(33.2, 90) * mm, "end": v(15.2, 108) * mm});
            skLineSegment(sketch, "E82", {"start": v(15.2, 108) * mm, "end": v(15.2, 120) * mm});
            skArc(sketch, "E83", {"start": v(15.2, 120) * mm, "mid": v(0.2, 135) * mm, "end": v(-14.8, 120) * mm});
            skCircle(sketch, "E84", {"center": v(0.2, 120) * mm, "radius": 6 * mm});
            skLineSegment(sketch, "E85", {"start": v(-32.61, -90) * mm, "end": v(-14.61, -108) * mm});
            skLineSegment(sketch, "E86", {"start": v(-14.61, -108) * mm, "end": v(-14.61, -120) * mm});
            skLineSegment(sketch, "E87", {"start": v(15.39, -120) * mm, "end": v(15.39, -108) * mm});
            skLineSegment(sketch, "E88", {"start": v(15.39, -108) * mm, "end": v(33.39, -90) * mm});
            skArc(sketch, "E89", {"start": v(-14.61, -120) * mm, "mid": v(0.39, -135) * mm, "end": v(15.39, -120) * mm});
            skCircle(sketch, "E90", {"center": v(0.39, -120) * mm, "radius": 6 * mm});
            skLineSegment(sketch, "E91", {"start": v(0.2, 120) * mm, "end": v(0.2, 90) * mm, "construction": true});
            skLineSegment(sketch, "E92", {"start": v(0.39, -120) * mm, "end": v(0.39, -90) * mm, "construction": true});
            skSolve(sketch);
        }
        {
            var Q0;
            {var subQ0=sQuery(id+"F16.wireOp",EDGE,"E79");Q0=makeQuery(id+"F16.imprint","IMPRINT",FACE,{"disambiguationData":[TD([[makeQuery(id+"F16.imprint","IMPRINT",EDGE,{"derivedFrom":subQ0}),-1.0]])]});}
            var Q1;
            {var subQ1=sQuery(id+"F16.wireOp",EDGE,"E85");Q1=makeQuery(id+"F16.imprint","IMPRINT",FACE,{"disambiguationData":[TD([[makeQuery(id+"F16.imprint","IMPRINT",EDGE,{"derivedFrom":subQ1}),1.0]])]});}
            var Q2;
            Q2=makeQuery(id+"F16.imprint","IMPRINT",FACE,{"disambiguationData":[TD([[makeQuery(id+"F16.imprint","IMPRINT",EDGE,{"derivedFrom":makeQuery(id+"F1.opExtrude","CAP_EDGE",EDGE,{"disambiguationData":[OSD([sQuery(id+"F0.wireOp",EDGE,"E1.left")])],"isStart":true})}),-1.0]])]});
            extrude(context, id + "F17", {"entities" : qUnion([Q0, Q1, Q2]), "depth" : 5 * mm, "symmetric" : true});
        }
    });
